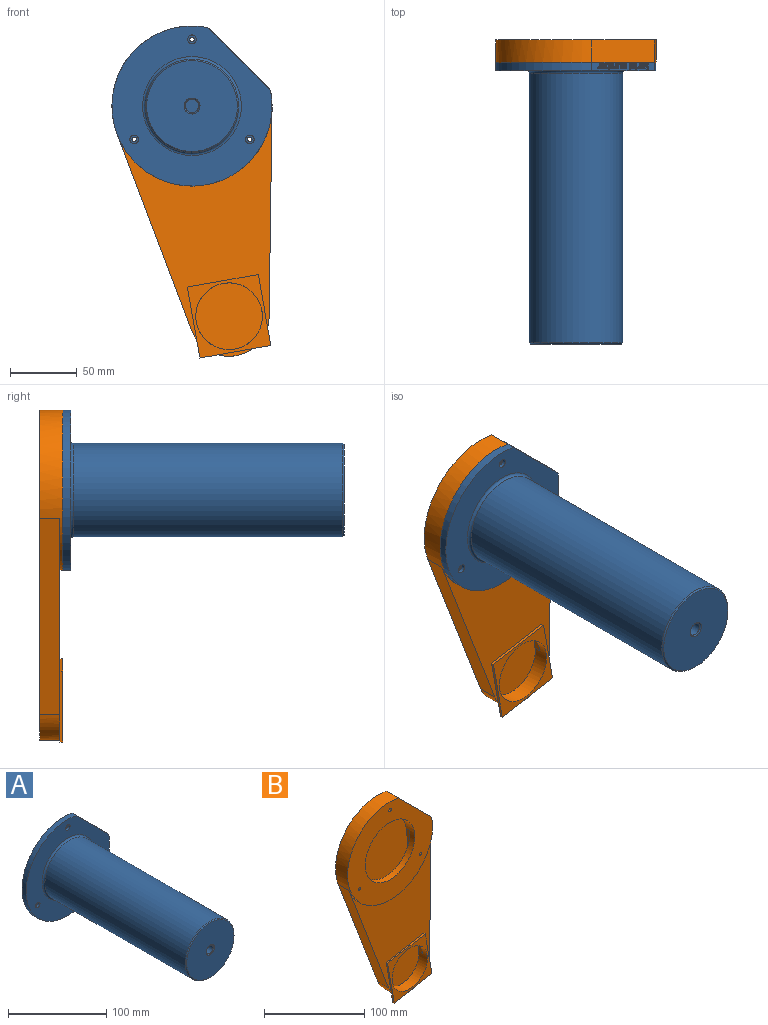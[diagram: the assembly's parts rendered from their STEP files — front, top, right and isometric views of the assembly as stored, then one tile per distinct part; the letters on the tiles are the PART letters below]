
ASSEMBLY  parts=2 mates=1
PART A: 267 faces, bbox 120x215x120 mm
  f0: plane 46.9x46.9mm, normal (0.71,0,0.71), area 268.5mm2, adj f7,f9,f10,f29,f30,f31,f32,f33
  f1: cylinder r=1.7mm len=3.4mm, axis (0,-1,0), area 32mm2, adj f2,f9
  f2: plane 6.5x6.5mm, normal (0,-1,0), area 24.1mm2, adj f1,f3
  f3: cylinder r=3.25mm len=6.5mm, axis (0,-1,0), area 61.3mm2, adj f2,f10
  f4: cylinder r=1.7mm len=3.4mm, axis (0,-1,0), area 32mm2, adj f5,f9
  f5: plane 6.5x6.5mm, normal (0,-1,0), area 24.1mm2, adj f4,f6
  f6: cylinder r=3.25mm len=6.5mm, axis (0,-1,0), area 61.3mm2, adj f5,f10
  f7: cylinder r=60mm len=120mm, axis (0,-1,0), area 1840.3mm2, adj f0,f9,f10
  f8: cylinder r=30mm len=204mm, axis (0,-1,0), area 38453.1mm2, adj f9,f19
  f9: plane 120x120mm, normal (0,1,0), area 8004.9mm2, adj f0,f1,f4,f7,f8,f26
  f10: plane 120x120mm, normal (0,-1,0), area 6459mm2, adj f0,f3,f6,f7,f18,f28,f41,f42
  f11: cylinder r=35mm len=202mm, axis (0,1,0), area 44422.1mm2, adj f18,f25
  f12: plane 56x56mm, normal (0,1,0), area 2309.1mm2, adj f15,f19
  f13: cylinder r=5mm len=199mm, axis (0,1,0), area 6251.8mm2, adj f17,f20
  f14: plane 68x68mm, normal (0,-1,0), area 3518.6mm2, adj f20,f25
  f15: cylinder r=7mm len=199mm, axis (0,1,0), area 8752.5mm2, adj f12,f21
  f16: plane 12x12mm, normal (0,1,0), area 34.6mm2, adj f21,f22
  f17: plane 10x10mm, normal (0,-1,0), area 78.5mm2, adj f13
  f18: torus R=37mm, axis (0,-1,0), area 705.2mm2, adj f10,f11
  f19: torus R=28mm, axis (0,-1,0), area 577.8mm2, adj f8,f12
  f20: cone r=5mm half-angle=45deg, axis (0,-1,0), area 48.9mm2, adj f13,f14
  f21: cone r=7mm half-angle=45deg, axis (0,-1,0), area 57.8mm2, adj f15,f16
  f22: cylinder r=5mm len=10mm, axis (0,-1,0), area 282.7mm2, adj f16,f24
  f23: plane 8x8mm, normal (0,1,0), area 50.3mm2, adj f24
  f24: cone r=5mm half-angle=45deg, axis (0,-1,0), area 40mm2, adj f22,f23
  f25: cone r=34mm half-angle=45deg, axis (0,1,0), area 306.6mm2, adj f11,f14
  f26: cylinder r=1.7mm len=3.4mm, axis (0,-1,0), area 32mm2, adj f9,f27
  f27: plane 6.5x6.5mm, normal (0,-1,0), area 24.1mm2, adj f26,f28
  f28: cylinder r=3.25mm len=6.5mm, axis (0,-1,0), area 61.3mm2, adj f10,f27
  f29: extruded ~1.19x0.42mm, area 0.1mm2, adj f0,f30,f56,f57
  f30: extruded ~0.92x0.24mm, area 0mm2, adj f0,f29,f31,f57
  f31: extruded ~0.79x0.79mm, area 0.1mm2, adj f0,f30,f32,f57
  f32: extruded ~0.56x0.56mm, area 0mm2, adj f0,f31,f33,f57
  f33: extruded ~0.22x0.2mm, area 0mm2, adj f0,f32,f34,f57
  f34: extruded ~0.27x0.09mm, area 0mm2, adj f0,f33,f35,f57
  f35: extruded ~0.41x0.16mm, area 0mm2, adj f0,f34,f36,f57
  f36: extruded ~0.4x0.4mm, area 0mm2, adj f0,f35,f37,f57
  f37: extruded ~0.44x0.44mm, area 0mm2, adj f0,f36,f38,f57
  f38: extruded ~0.56x0.56mm, area 0mm2, adj f0,f37,f39,f57
  f39: plane 0.92x0.3mm, normal (-0.65,0.38,0.65), area 0mm2, adj f0,f38,f40,f57
  f40: extruded ~0.62x0.62mm, area 0mm2, adj f0,f39,f41,f57
  f41: extruded ~0.65x0.65mm, area 0.1mm2, adj f0,f10,f40,f42,f57,f58
  f42: extruded ~1.05x1.05mm, area 0.1mm2, adj f0,f10,f41,f43,f57,f58
  f43: extruded ~1.16x0.39mm, area 0.1mm2, adj f0,f42,f44,f57
  f44: extruded ~0.68x0.14mm, area 0mm2, adj f0,f43,f45,f57
  f45: extruded ~0.51x0.32mm, area 0mm2, adj f0,f44,f46,f57
  f46: extruded ~0.57x0.57mm, area 0mm2, adj f0,f45,f47,f57
  f47: extruded ~0.54x0.54mm, area 0mm2, adj f0,f46,f48,f57
  f48: extruded ~0.25x0.23mm, area 0mm2, adj f0,f47,f49,f57
  f49: extruded ~0.29x0.1mm, area 0mm2, adj f0,f48,f50,f57
  f50: extruded ~0.44x0.18mm, area 0mm2, adj f0,f49,f51,f57
  f51: extruded ~0.46x0.46mm, area 0mm2, adj f0,f50,f52,f57
  f52: extruded ~0.54x0.54mm, area 0mm2, adj f0,f51,f53,f57
  f53: extruded ~0.71x0.71mm, area 0.1mm2, adj f0,f52,f54,f57
  f54: plane 1.09x0.04mm, normal (0.71,0,-0.71), area 0.1mm2, adj f0,f53,f55,f57
  f55: extruded ~1.15x1.15mm, area 0.1mm2, adj f0,f54,f56,f57
  f56: extruded ~1.1x1.1mm, area 0.1mm2, adj f0,f29,f55,f57
  f57: plane 5.71x2.56mm, normal (0.71,0,0.71), area 11.6mm2, adj f29,f30,f31,f32,f33,f34,f35,f36
  f58: plane 0.66x0.66mm, normal (-0.71,0,-0.71), area 0mm2, adj f10,f41,f42
  f59: extruded ~1.17x1.17mm, area 0.1mm2, adj f0,f60,f78,f79
  f60: extruded ~0.63x0.63mm, area 0mm2, adj f0,f59,f61,f79
  f61: extruded ~0.49x0.49mm, area 0mm2, adj f0,f60,f62,f79
  f62: plane 0.9x0.04mm, normal (-0.71,0,0.71), area 0mm2, adj f0,f61,f63,f79
  f63: extruded ~0.54x0.54mm, area 0mm2, adj f0,f62,f64,f79
  f64: extruded ~0.55x0.55mm, area 0mm2, adj f0,f63,f65,f79
  f65: extruded ~0.58x0.58mm, area 0mm2, adj f0,f64,f66,f79
  f66: extruded ~0.77x0.24mm, area 0mm2, adj f0,f65,f67,f79
  f67: plane 1.97x1.97mm, normal (0,1,0), area 0.1mm2, adj f0,f66,f68,f79
  f68: plane 0.56x0.04mm, normal (-0.71,0,0.71), area 0mm2, adj f0,f67,f69,f79
  f69: extruded ~1.42x0.39mm, area 0.1mm2, adj f0,f68,f70,f79
  f70: extruded ~1.03x1.03mm, area 0.1mm2, adj f0,f69,f71,f79
  f71: extruded ~1.08x1.08mm, area 0.1mm2, adj f0,f70,f72,f79
  f72: extruded ~1.65x0.41mm, area 0.1mm2, adj f0,f71,f78,f79
  f73: extruded ~0.44x0.44mm, area 0mm2, adj f74,f77,f79,f80
  f74: extruded ~0.45x0.45mm, area 0mm2, adj f73,f75,f79,f80
  f75: extruded ~0.66x0.19mm, area 0mm2, adj f74,f76,f79,f80
  f76: plane 1.19x1.19mm, normal (0,-1,0), area 0.1mm2, adj f75,f77,f79,f80
  f77: extruded ~0.66x0.2mm, area 0mm2, adj f73,f76,f79,f80
  f78: extruded ~1.6x0.44mm, area 0.1mm2, adj f0,f59,f72,f79
  f79: plane 4.4x2.77mm, normal (0.71,0,0.71), area 10.9mm2, adj f59,f60,f61,f62,f63,f64,f65,f66
  f80: plane 1.15x1.15mm, normal (0.71,0,0.71), area 1.2mm2, adj f73,f74,f75,f76,f77
  f81: extruded ~0.31x0.31mm, area 0mm2, adj f0,f82,f93,f94
  f82: extruded ~0.55x0.55mm, area 0mm2, adj f0,f81,f83,f94
  f83: extruded ~0.58x0.41mm, area 0mm2, adj f0,f82,f84,f94
  f84: plane 0.08x0.08mm, normal (0,-1,0), area 0mm2, adj f0,f83,f85,f94
  f85: plane 0.71x0.16mm, normal (-0.69,-0.23,0.69), area 0mm2, adj f0,f84,f86,f94
  f86: plane 0.66x0.66mm, normal (0,-1,0), area 0mm2, adj f0,f85,f87,f94
  f87: plane 4.25x0.04mm, normal (0.71,0,-0.71), area 0.2mm2, adj f0,f86,f88,f94
  f88: plane 0.85x0.85mm, normal (0,1,0), area 0.1mm2, adj f0,f87,f89,f94
  f89: plane 2.16x0.04mm, normal (-0.71,0,0.71), area 0.1mm2, adj f0,f88,f90,f94
  f90: extruded ~0.8x0.25mm, area 0mm2, adj f0,f89,f91,f94
  f91: extruded ~0.65x0.65mm, area 0mm2, adj f0,f90,f92,f94
  f92: extruded ~0.28x0.28mm, area 0mm2, adj f0,f91,f93,f94
  f93: plane 1.09x0.1mm, normal (-0.7,0.08,0.7), area 0.1mm2, adj f0,f81,f92,f94
  f94: plane 4.33x1.95mm, normal (0.71,0,0.71), area 6.4mm2, adj f81,f82,f83,f84,f85,f86,f87,f88
  f95: extruded ~0.57x0.52mm, area 0.1mm2, adj f0,f10,f96,f99,f100,f101
  f96: extruded ~0.57x0.48mm, area 0mm2, adj f0,f95,f97,f100
  f97: extruded ~0.37x0.37mm, area 0mm2, adj f0,f96,f98,f100
  f98: extruded ~0.42x0.15mm, area 0mm2, adj f0,f97,f99,f100
  f99: extruded ~0.57x0.52mm, area 0.1mm2, adj f0,f10,f95,f98,f100,f101
  f100: plane 1.14x0.89mm, normal (0.71,0,0.71), area 1.2mm2, adj f95,f96,f97,f98,f99
  f101: plane 0.89x0.89mm, normal (-0.71,0,-0.71), area 0.3mm2, adj f10,f95,f99
  f102: plane 0.85x0.85mm, normal (0,1,0), area 0.1mm2, adj f0,f103,f105,f106
  f103: plane 4.25x0.04mm, normal (-0.71,0,0.71), area 0.2mm2, adj f0,f102,f104,f106
  f104: plane 0.85x0.85mm, normal (0,-1,0), area 0.1mm2, adj f0,f103,f105,f106
  f105: plane 4.25x0.04mm, normal (0.71,0,-0.71), area 0.2mm2, adj f0,f102,f104,f106
  f106: plane 4.25x0.82mm, normal (0.71,0,0.71), area 4.9mm2, adj f102,f103,f104,f105
  f107: plane 0.35x0.35mm, normal (-0.02,1,0.02), area 0mm2, adj f108,f131,f132,f133
  f108: plane 0.35x0.04mm, normal (0.71,0,-0.71), area 0mm2, adj f107,f109,f132,f133
  f109: extruded ~0.62x0.21mm, area 0mm2, adj f108,f110,f132,f133
  f110: extruded ~0.49x0.49mm, area 0mm2, adj f109,f111,f132,f133
  f111: extruded ~0.49x0.43mm, area 0mm2, adj f110,f112,f132,f133
  f112: extruded ~0.51x0.21mm, area 0mm2, adj f111,f131,f132,f133
  f113: plane 0.58x0.19mm, normal (0.66,0.36,-0.66), area 0mm2, adj f0,f114,f130,f132
  f114: plane 0.61x0.61mm, normal (0,1,0), area 0mm2, adj f0,f113,f115,f132
  f115: plane 2.83x0.04mm, normal (-0.71,0,0.71), area 0.1mm2, adj f0,f114,f116,f132
  f116: extruded ~1.13x0.36mm, area 0.1mm2, adj f0,f115,f117,f132
  f117: extruded ~0.96x0.96mm, area 0.1mm2, adj f0,f116,f118,f132
  f118: extruded ~1.18x1.18mm, area 0.1mm2, adj f0,f117,f119,f132
  f119: plane 0.78x0.31mm, normal (0.64,0.44,-0.64), area 0mm2, adj f0,f118,f120,f132
  f120: extruded ~0.88x0.88mm, area 0.1mm2, adj f0,f119,f121,f132
  f121: extruded ~0.65x0.5mm, area 0.1mm2, adj f0,f120,f122,f132
  f122: plane 0.19x0.04mm, normal (0.71,0,-0.71), area 0mm2, adj f0,f121,f123,f132
  f123: plane 0.56x0.56mm, normal (0.02,-1,-0.02), area 0mm2, adj f0,f122,f124,f132
  f124: extruded ~1.04x1.04mm, area 0.1mm2, adj f0,f123,f125,f132
  f125: extruded ~1x0.37mm, area 0.1mm2, adj f0,f124,f126,f132
  f126: extruded ~1x0.28mm, area 0.1mm2, adj f0,f125,f127,f132
  f127: extruded ~0.72x0.72mm, area 0.1mm2, adj f0,f126,f128,f132
  f128: extruded ~0.61x0.61mm, area 0mm2, adj f0,f127,f129,f132
  f129: extruded ~0.51x0.46mm, area 0mm2, adj f0,f128,f130,f132
  f130: plane 0.06x0.06mm, normal (0,1,0), area 0mm2, adj f0,f113,f129,f132
  f131: extruded ~0.57x0.57mm, area 0mm2, adj f107,f112,f132,f133
  f132: plane 4.41x2.68mm, normal (0.71,0,0.71), area 11mm2, adj f107,f108,f109,f110,f111,f112,f113,f114
  f133: plane 1.2x1.02mm, normal (0.71,0,0.71), area 1.4mm2, adj f107,f108,f109,f110,f111,f112,f131
  f134: plane 0.85x0.85mm, normal (0,1,0), area 0.1mm2, adj f0,f135,f137,f138
  f135: plane 5.91x0.07mm, normal (-0.71,0,0.71), area 0.3mm2, adj f0,f10,f134,f136,f138,f139
  f136: plane 0.89x0.89mm, normal (0,-1,0), area 0.1mm2, adj f135,f137,f138,f139
  f137: plane 5.91x0.07mm, normal (0.71,0,-0.71), area 0.3mm2, adj f0,f10,f134,f136,f138,f139
  f138: plane 5.91x0.82mm, normal (0.71,0,0.71), area 6.8mm2, adj f134,f135,f136,f137
  f139: plane 0.82x0.82mm, normal (-0.71,0,-0.71), area 0.4mm2, adj f10,f135,f136,f137
  f140: plane 0.85x0.85mm, normal (0,1,0), area 0.1mm2, adj f0,f141,f156,f157
  f141: plane 2.77x0.04mm, normal (-0.71,0,0.71), area 0.1mm2, adj f0,f140,f142,f157
  f142: extruded ~1.16x0.31mm, area 0.1mm2, adj f0,f141,f143,f157
  f143: extruded ~0.83x0.83mm, area 0.1mm2, adj f0,f142,f144,f157
  f144: extruded ~0.58x0.58mm, area 0mm2, adj f0,f143,f145,f157
  f145: extruded ~0.47x0.41mm, area 0mm2, adj f0,f144,f146,f157
  f146: plane 0.08x0.08mm, normal (0,-1,0), area 0mm2, adj f0,f145,f147,f157
  f147: plane 0.54x0.15mm, normal (-0.68,-0.28,0.68), area 0mm2, adj f0,f146,f148,f157
  f148: plane 0.66x0.66mm, normal (0,-1,0), area 0mm2, adj f0,f147,f149,f157
  f149: plane 4.25x0.04mm, normal (0.71,0,-0.71), area 0.2mm2, adj f0,f148,f150,f157
  f150: plane 0.85x0.85mm, normal (0,1,0), area 0.1mm2, adj f0,f149,f151,f157
  f151: plane 2x0.04mm, normal (-0.71,0,0.71), area 0.1mm2, adj f0,f150,f152,f157
  f152: extruded ~1.08x0.19mm, area 0.1mm2, adj f0,f151,f153,f157
  f153: extruded ~0.53x0.53mm, area 0mm2, adj f0,f152,f154,f157
  f154: extruded ~0.4x0.4mm, area 0mm2, adj f0,f153,f155,f157
  f155: extruded ~0.69x0.15mm, area 0mm2, adj f0,f154,f156,f157
  f156: plane 2.48x0.04mm, normal (0.71,0,-0.71), area 0.1mm2, adj f0,f140,f155,f157
  f157: plane 4.33x2.77mm, normal (0.71,0,0.71), area 11mm2, adj f140,f141,f142,f143,f144,f145,f146,f147
  f158: plane 0.54x0.15mm, normal (0.68,0.28,-0.68), area 0mm2, adj f0,f159,f174,f175
  f159: plane 0.66x0.66mm, normal (0,1,0), area 0mm2, adj f0,f158,f160,f175
  f160: plane 4.25x0.04mm, normal (-0.71,0,0.71), area 0.2mm2, adj f0,f159,f161,f175
  f161: plane 0.85x0.85mm, normal (0,-1,0), area 0.1mm2, adj f0,f160,f162,f175
  f162: plane 2x0.04mm, normal (0.71,0,-0.71), area 0.1mm2, adj f0,f161,f163,f175
  f163: extruded ~1.08x0.19mm, area 0.1mm2, adj f0,f162,f164,f175
  f164: extruded ~0.53x0.53mm, area 0mm2, adj f0,f163,f165,f175
  f165: extruded ~0.4x0.4mm, area 0mm2, adj f0,f164,f166,f175
  f166: extruded ~0.69x0.15mm, area 0mm2, adj f0,f165,f167,f175
  f167: plane 2.48x0.04mm, normal (-0.71,0,0.71), area 0.1mm2, adj f0,f166,f168,f175
  f168: plane 0.85x0.85mm, normal (0,-1,0), area 0.1mm2, adj f0,f167,f169,f175
  f169: plane 2.77x0.04mm, normal (0.71,0,-0.71), area 0.1mm2, adj f0,f168,f170,f175
  f170: extruded ~1.15x0.3mm, area 0.1mm2, adj f0,f169,f171,f175
  f171: extruded ~0.83x0.83mm, area 0.1mm2, adj f0,f170,f172,f175
  f172: extruded ~0.59x0.59mm, area 0mm2, adj f0,f171,f173,f175
  f173: extruded ~0.46x0.41mm, area 0mm2, adj f0,f172,f174,f175
  f174: plane 0.08x0.08mm, normal (0,1,0), area 0mm2, adj f0,f158,f173,f175
  f175: plane 4.32x2.77mm, normal (0.71,0,0.71), area 11mm2, adj f158,f159,f160,f161,f162,f163,f164,f165
  f176: plane 0.85x0.85mm, normal (0,1,0), area 0.1mm2, adj f0,f177,f203,f204
  f177: plane 2.13x0.04mm, normal (-0.71,0,0.71), area 0.1mm2, adj f0,f176,f178,f204
  f178: extruded ~0.97x0.18mm, area 0.1mm2, adj f0,f177,f179,f204
  f179: extruded ~0.49x0.49mm, area 0mm2, adj f0,f178,f180,f204
  f180: extruded ~0.38x0.38mm, area 0mm2, adj f0,f179,f181,f204
  f181: extruded ~0.69x0.14mm, area 0mm2, adj f0,f180,f182,f204
  f182: plane 2.48x0.04mm, normal (0.71,0,-0.71), area 0.1mm2, adj f0,f181,f183,f204
  f183: plane 0.86x0.86mm, normal (0,1,0), area 0.1mm2, adj f0,f182,f184,f204
  f184: plane 2.77x0.04mm, normal (-0.71,0,0.71), area 0.1mm2, adj f0,f183,f185,f204
  f185: extruded ~1.19x0.3mm, area 0.1mm2, adj f0,f184,f186,f204
  f186: extruded ~0.81x0.81mm, area 0.1mm2, adj f0,f185,f187,f204
  f187: extruded ~0.57x0.57mm, area 0mm2, adj f0,f186,f188,f204
  f188: extruded ~0.46x0.39mm, area 0mm2, adj f0,f187,f189,f204
  f189: plane 0.11x0.11mm, normal (0,-1,0), area 0mm2, adj f0,f188,f190,f204
  f190: extruded ~0.95x0.95mm, area 0.1mm2, adj f0,f189,f191,f204
  f191: extruded ~0.56x0.56mm, area 0mm2, adj f0,f190,f192,f204
  f192: extruded ~0.46x0.38mm, area 0mm2, adj f0,f191,f193,f204
  f193: plane 0.08x0.08mm, normal (0,-1,0), area 0mm2, adj f0,f192,f194,f204
  f194: plane 0.54x0.15mm, normal (-0.68,-0.28,0.68), area 0mm2, adj f0,f193,f195,f204
  f195: plane 0.66x0.66mm, normal (0,-1,0), area 0mm2, adj f0,f194,f196,f204
  f196: plane 4.25x0.04mm, normal (0.71,0,-0.71), area 0.2mm2, adj f0,f195,f197,f204
  f197: plane 0.85x0.85mm, normal (0,1,0), area 0.1mm2, adj f0,f196,f198,f204
  f198: plane 2x0.04mm, normal (-0.71,0,0.71), area 0.1mm2, adj f0,f197,f199,f204
  f199: extruded ~1.07x0.18mm, area 0.1mm2, adj f0,f198,f200,f204
  f200: extruded ~0.49x0.49mm, area 0mm2, adj f0,f199,f201,f204
  f201: extruded ~0.38x0.38mm, area 0mm2, adj f0,f200,f202,f204
  f202: extruded ~0.69x0.14mm, area 0mm2, adj f0,f201,f203,f204
  f203: plane 2.48x0.04mm, normal (0.71,0,-0.71), area 0.1mm2, adj f0,f176,f202,f204
  f204: plane 4.56x4.56mm, normal (0.71,0,0.71), area 17.1mm2, adj f176,f177,f178,f179,f180,f181,f182,f183
  f205: extruded ~0.48x0.48mm, area 0mm2, adj f206,f227,f228,f230
  f206: extruded ~0.45x0.45mm, area 0mm2, adj f205,f207,f228,f230
  f207: extruded ~0.94x0.19mm, area 0mm2, adj f206,f208,f228,f230
  f208: extruded ~0.96x0.18mm, area 0mm2, adj f207,f209,f228,f230
  f209: extruded ~0.44x0.44mm, area 0mm2, adj f208,f210,f228,f230
  f210: extruded ~0.49x0.49mm, area 0mm2, adj f209,f211,f228,f230
  f211: extruded ~0.98x0.18mm, area 0.1mm2, adj f210,f212,f228,f230
  f212: plane 0.13x0.04mm, normal (-0.71,0,0.71), area 0mm2, adj f211,f227,f228,f230
  f213: extruded ~0.87x0.87mm, area 0.1mm2, adj f0,f214,f226,f228
  f214: extruded ~0.89x0.89mm, area 0.1mm2, adj f0,f213,f215,f228
  f215: plane 0.07x0.07mm, normal (0,-1,0), area 0mm2, adj f0,f214,f216,f228
  f216: extruded ~0.84x0.07mm, area 0mm2, adj f0,f215,f217,f228
  f217: plane 1.38x0.07mm, normal (-0.71,0,0.71), area 0.1mm2, adj f0,f10,f216,f218,f228,f229
  f218: plane 0.89x0.89mm, normal (0,-1,0), area 0.1mm2, adj f217,f219,f228,f229
  f219: plane 5.91x0.07mm, normal (0.71,0,-0.71), area 0.3mm2, adj f0,f10,f218,f220,f228,f229
  f220: plane 0.66x0.66mm, normal (0,1,0), area 0mm2, adj f0,f219,f221,f228
  f221: plane 0.47x0.17mm, normal (-0.65,0.38,0.65), area 0mm2, adj f0,f220,f222,f228
  f222: plane 0.09x0.09mm, normal (0,1,0), area 0mm2, adj f0,f221,f223,f228
  f223: extruded ~0.87x0.87mm, area 0.1mm2, adj f0,f222,f224,f228
  f224: extruded ~0.88x0.88mm, area 0.1mm2, adj f0,f223,f225,f228
  f225: extruded ~1.63x0.35mm, area 0.1mm2, adj f0,f224,f226,f228
  f226: extruded ~1.61x0.34mm, area 0.1mm2, adj f0,f213,f225,f228
  f227: extruded ~0.87x0.18mm, area 0mm2, adj f205,f212,f228,f230
  f228: plane 5.99x2.8mm, normal (0.71,0,0.71), area 14mm2, adj f205,f206,f207,f208,f209,f210,f211,f212
  f229: plane 0.82x0.82mm, normal (-0.71,0,-0.71), area 0.4mm2, adj f10,f217,f218,f219
  f230: plane 2.54x1.15mm, normal (0.71,0,0.71), area 3.5mm2, adj f205,f206,f207,f208,f209,f210,f211,f212
  f231: extruded ~1.17x1.17mm, area 0.1mm2, adj f0,f232,f250,f251
  f232: extruded ~0.63x0.63mm, area 0mm2, adj f0,f231,f233,f251
  f233: extruded ~0.49x0.49mm, area 0mm2, adj f0,f232,f234,f251
  f234: plane 0.9x0.04mm, normal (-0.71,0,0.71), area 0mm2, adj f0,f233,f235,f251
  f235: extruded ~0.54x0.54mm, area 0mm2, adj f0,f234,f236,f251
  f236: extruded ~0.55x0.55mm, area 0mm2, adj f0,f235,f237,f251
  f237: extruded ~0.58x0.58mm, area 0mm2, adj f0,f236,f238,f251
  f238: extruded ~0.77x0.24mm, area 0mm2, adj f0,f237,f239,f251
  f239: plane 1.97x1.97mm, normal (0,1,0), area 0.1mm2, adj f0,f238,f240,f251
  f240: plane 0.56x0.04mm, normal (-0.71,0,0.71), area 0mm2, adj f0,f239,f241,f251
  f241: extruded ~1.42x0.39mm, area 0.1mm2, adj f0,f240,f242,f251
  f242: extruded ~1.03x1.03mm, area 0.1mm2, adj f0,f241,f243,f251
  f243: extruded ~1.08x1.08mm, area 0.1mm2, adj f0,f242,f244,f251
  f244: extruded ~1.65x0.41mm, area 0.1mm2, adj f0,f243,f250,f251
  f245: extruded ~0.44x0.44mm, area 0mm2, adj f246,f249,f251,f252
  f246: extruded ~0.45x0.45mm, area 0mm2, adj f245,f247,f251,f252
  f247: extruded ~0.66x0.19mm, area 0mm2, adj f246,f248,f251,f252
  f248: plane 1.19x1.19mm, normal (0,-1,0), area 0.1mm2, adj f247,f249,f251,f252
  f249: extruded ~0.66x0.2mm, area 0mm2, adj f245,f248,f251,f252
  f250: extruded ~1.6x0.44mm, area 0.1mm2, adj f0,f231,f244,f251
  f251: plane 4.4x2.77mm, normal (0.71,0,0.71), area 10.9mm2, adj f231,f232,f233,f234,f235,f236,f237,f238
  f252: plane 1.15x1.15mm, normal (0.71,0,0.71), area 1.2mm2, adj f245,f246,f247,f248,f249
  f253: extruded ~0.31x0.31mm, area 0mm2, adj f0,f254,f265,f266
  f254: extruded ~0.55x0.55mm, area 0mm2, adj f0,f253,f255,f266
  f255: extruded ~0.58x0.41mm, area 0mm2, adj f0,f254,f256,f266
  f256: plane 0.08x0.08mm, normal (0,-1,0), area 0mm2, adj f0,f255,f257,f266
  f257: plane 0.71x0.16mm, normal (-0.69,-0.23,0.69), area 0mm2, adj f0,f256,f258,f266
  f258: plane 0.66x0.66mm, normal (0,-1,0), area 0mm2, adj f0,f257,f259,f266
  f259: plane 4.25x0.04mm, normal (0.71,0,-0.71), area 0.2mm2, adj f0,f258,f260,f266
  f260: plane 0.85x0.85mm, normal (0,1,0), area 0.1mm2, adj f0,f259,f261,f266
  f261: plane 2.16x0.04mm, normal (-0.71,0,0.71), area 0.1mm2, adj f0,f260,f262,f266
  f262: extruded ~0.8x0.25mm, area 0mm2, adj f0,f261,f263,f266
  f263: extruded ~0.65x0.65mm, area 0mm2, adj f0,f262,f264,f266
  f264: extruded ~0.28x0.28mm, area 0mm2, adj f0,f263,f265,f266
  f265: plane 1.09x0.1mm, normal (-0.7,0.08,0.7), area 0.1mm2, adj f0,f253,f264,f266
  f266: plane 4.33x1.95mm, normal (0.71,0,0.71), area 6.4mm2, adj f253,f254,f255,f256,f257,f258,f259,f260
PART B: 25 faces, bbox 120x17x248.8 mm
  f0: cylinder r=1.7mm len=17mm, axis (0,-1,0), area 181.6mm2, adj f2,f11
  f1: cylinder r=1.7mm len=17mm, axis (0,-1,0), area 181.6mm2, adj f2,f11
  f2: plane 120x120mm, normal (0,-1,0), area 6983.9mm2, adj f0,f1,f4,f12,f13,f24
  f3: plane 25.76x5.68mm, normal (0,-1,0), area 52.9mm2, adj f15,f18
  f4: cylinder r=35mm len=70mm, axis (0,-1,0), area 2111mm2, adj f2,f5,f7,f8,f9
  f5: plane 155.22x37.5mm, normal (0.97,0,0.23), area 798.4mm2, adj f4,f6,f8,f9
  f6: cylinder r=25mm len=50mm, axis (0,-1,0), area 1476.6mm2, adj f5,f7,f8,f9,f22
  f7: plane 158.69x17.85mm, normal (-0.99,0,-0.11), area 798.4mm2, adj f4,f6,f8,f9
  f8: plane 217.57x87.78mm, normal (0,-1,0), area 12524.7mm2, adj f4,f5,f6,f7
  f9: plane 167.35x86.65mm, normal (0,1,0), area 6712.8mm2, adj f4,f5,f6,f7
  f10: plane 174.29x116.08mm, normal (0,-1,0), area 7593.9mm2, adj f13,f14,f15,f16,f19,f20,f21
  f11: plane 247.57x120mm, normal (0,1,0), area 21245.1mm2, adj f0,f1,f12,f13,f14,f15,f16,f24
  f12: plane 46.9x46.9mm, normal (0.71,0,0.71), area 1127.7mm2, adj f2,f11,f13
  f13: cylinder r=60mm len=120mm, axis (0,1,0), area 2726.1mm2, adj f2,f10,f11,f12,f14,f16
  f14: plane 157.15x15mm, normal (1,0,-0.01), area 2357.4mm2, adj f10,f11,f13,f15
  f15: cylinder r=30mm len=58.04mm, axis (0,1,0), area 1244mm2, adj f3,f10,f11,f14,f16,f17,f23
  f16: plane 146.91x55.83mm, normal (-0.93,0,-0.36), area 2357.4mm2, adj f10,f11,f13,f15
  f17: plane 16.13x13.71mm, normal (0,1,0), area 75mm2, adj f15,f18,f19
  f18: plane 53.18x9.38mm, normal (0.17,0,-0.98), area 108mm2, adj f3,f17,f19,f21,f22,f23
  f19: plane 53.18x9.38mm, normal (0.98,0,0.17), area 108mm2, adj f10,f17,f18,f20,f22
  f20: plane 53.18x9.38mm, normal (-0.17,0,0.98), area 108mm2, adj f10,f19,f21,f22
  f21: plane 53.18x9.38mm, normal (-0.98,0,-0.17), area 108mm2, adj f10,f18,f20,f22,f23
  f22: plane 62.56x62.56mm, normal (0,-1,0), area 952.5mm2, adj f6,f18,f19,f20,f21
  f23: plane 16.13x13.71mm, normal (0,1,0), area 75mm2, adj f15,f18,f21
  f24: cylinder r=1.7mm len=17mm, axis (0,-1,0), area 181.6mm2, adj f2,f11
PLACE A t=(-69.89,7.79,-39.54)mm
PLACE B t=(-69.89,30.79,-39.54)mm fixed
MATE fastened A.f26 <-> B.f24  axis (0,1,0) through (-69.89,13.79,10.46)mm
